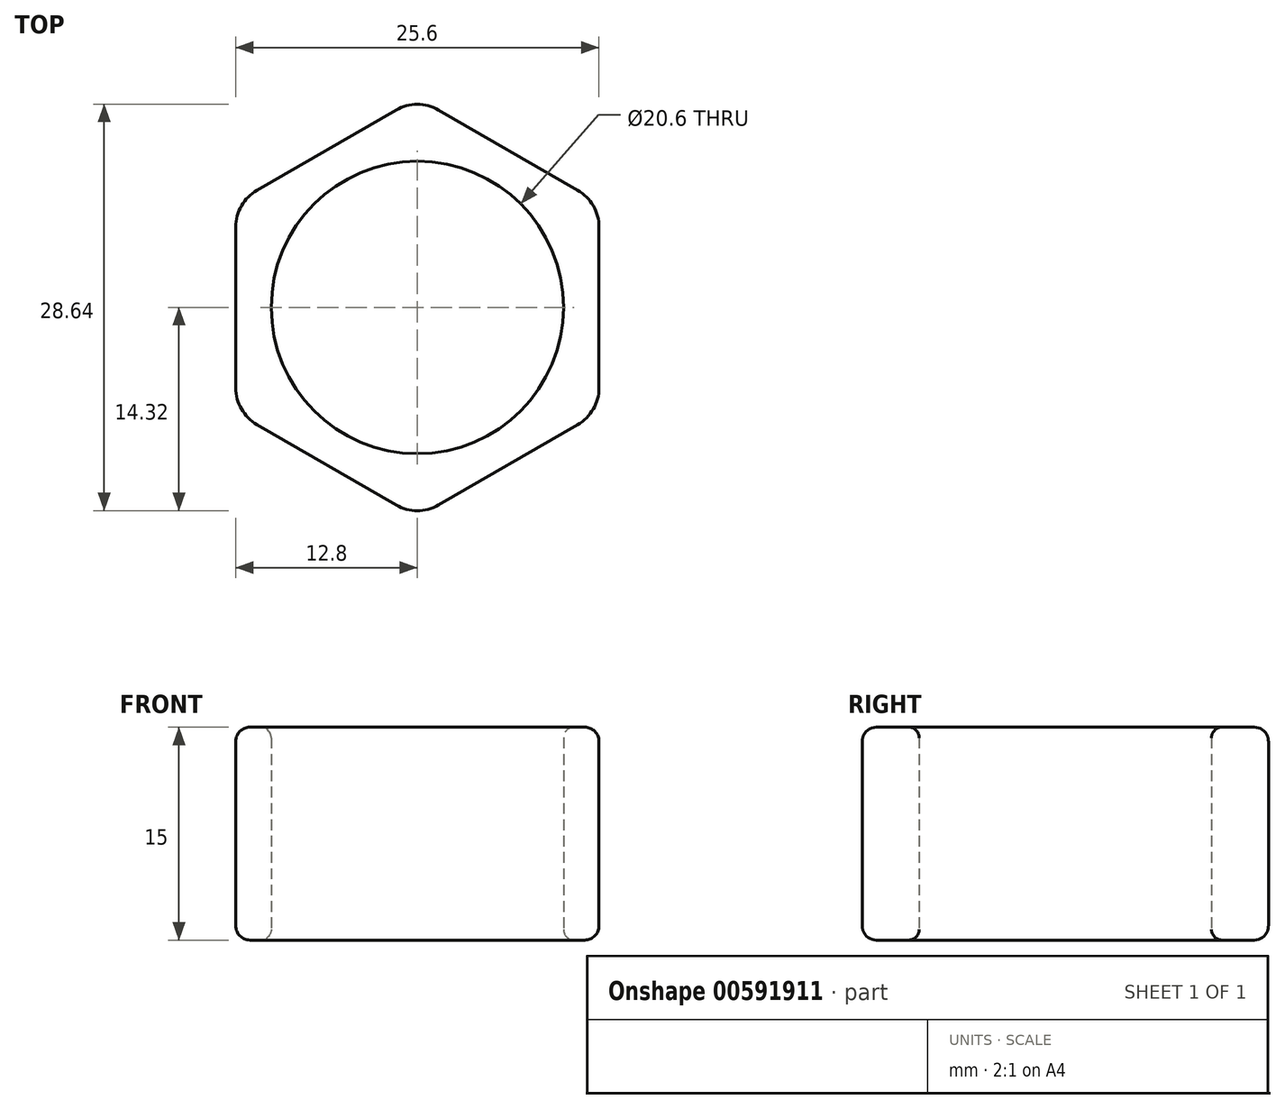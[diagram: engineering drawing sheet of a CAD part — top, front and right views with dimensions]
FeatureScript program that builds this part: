
annotation { "Feature Type Name" : "Feature", "Feature Type Description" : "" }
export const myFeature = defineFeature(function(context is Context, id is Id, definition is map)
    precondition{}
    {
        {
            var Q0;
            Q0=qCreatedBy(makeId("Top.planeOp"),FACE);
            var sketch = newSketch(context, id + "F0", { "sketchPlane" : qUnion([Q0])});
            skCircle(sketch, "E0", {"center": v(0, 0) * mm, "radius": 10.3 * mm});
            skCircle(sketch, "E1.0", {"center": v(0, 0) * mm, "radius": 12.8 * mm});
            skCircle(sketch, "E2.cCircle", {"center": v(0, 0) * mm, "radius": 12.8 * mm, "construction": true});
            skLineSegment(sketch, "E2.0", {"start": v(12.8, 7.4) * mm, "end": v(12.8, -7.4) * mm});
            skLineSegment(sketch, "E2.1", {"start": v(12.8, -7.4) * mm, "end": v(0, -14.78) * mm});
            skLineSegment(sketch, "E2.2", {"start": v(0, -14.78) * mm, "end": v(-12.8, -7.4) * mm});
            skLineSegment(sketch, "E2.3", {"start": v(-12.8, -7.4) * mm, "end": v(-12.8, 7.4) * mm});
            skLineSegment(sketch, "E2.4", {"start": v(-12.8, 7.4) * mm, "end": v(0, 14.78) * mm});
            skLineSegment(sketch, "E2.5", {"start": v(0, 14.78) * mm, "end": v(12.8, 7.4) * mm});
            skPoint(sketch, "E2.0.midPoint", {"position": v(12.8, 0) * mm});
            skSolve(sketch);
        }
        {
            var Q0;
            {var subQ0=sQuery(id+"F0.wireOp",EDGE,"E2.5");var subQ1=sQuery(id+"F0.wireOp",EDGE,"E1.0");var subQ2=makeQuery(id+"F0.imprint","INTERSECT",VERTEX,{"derivedFrom":[subQ1,subQ0]});Q0=makeQuery(id+"F0.imprint","IMPRINT",FACE,{"disambiguationData":[TD([[makeQuery(id+"F0.imprint","IMPRINT",EDGE,{"disambiguationData":[TD([[subQ2,1.0]])],"derivedFrom":subQ1}),-1.0]])]});}
            var Q1;
            {var subQ0=sQuery(id+"F0.wireOp",EDGE,"E2.5");var subQ1=sQuery(id+"F0.wireOp",EDGE,"E1.0");var subQ2=makeQuery(id+"F0.imprint","INTERSECT",VERTEX,{"derivedFrom":[subQ1,subQ0]});Q1=makeQuery(id+"F0.imprint","IMPRINT",FACE,{"disambiguationData":[TD([[makeQuery(id+"F0.imprint","IMPRINT",EDGE,{"disambiguationData":[TD([[subQ2,-1.0]])],"derivedFrom":subQ1}),-1.0]])]});}
            var Q2;
            {var subQ0=sQuery(id+"F0.wireOp",EDGE,"E2.4");var subQ1=sQuery(id+"F0.wireOp",EDGE,"E1.0");var subQ2=makeQuery(id+"F0.imprint","INTERSECT",VERTEX,{"derivedFrom":[subQ1,subQ0]});Q2=makeQuery(id+"F0.imprint","IMPRINT",FACE,{"disambiguationData":[TD([[makeQuery(id+"F0.imprint","IMPRINT",EDGE,{"disambiguationData":[TD([[subQ2,-1.0]])],"derivedFrom":subQ1}),-1.0]])]});}
            var Q3;
            {var subQ0=sQuery(id+"F0.wireOp",EDGE,"E2.3");var subQ1=sQuery(id+"F0.wireOp",EDGE,"E1.0");var subQ2=makeQuery(id+"F0.imprint","INTERSECT",VERTEX,{"derivedFrom":[subQ1,subQ0]});Q3=makeQuery(id+"F0.imprint","IMPRINT",FACE,{"disambiguationData":[TD([[makeQuery(id+"F0.imprint","IMPRINT",EDGE,{"disambiguationData":[TD([[subQ2,-1.0]])],"derivedFrom":subQ1}),-1.0]])]});}
            var Q4;
            {var subQ0=sQuery(id+"F0.wireOp",EDGE,"E2.2");var subQ1=sQuery(id+"F0.wireOp",EDGE,"E1.0");var subQ2=makeQuery(id+"F0.imprint","INTERSECT",VERTEX,{"derivedFrom":[subQ1,subQ0]});Q4=makeQuery(id+"F0.imprint","IMPRINT",FACE,{"disambiguationData":[TD([[makeQuery(id+"F0.imprint","IMPRINT",EDGE,{"disambiguationData":[TD([[subQ2,-1.0]])],"derivedFrom":subQ1}),-1.0]])]});}
            var Q5;
            {var subQ0=sQuery(id+"F0.wireOp",EDGE,"E2.0");var subQ1=sQuery(id+"F0.wireOp",EDGE,"E1.0");var subQ2=makeQuery(id+"F0.imprint","INTERSECT",VERTEX,{"derivedFrom":[subQ1,subQ0]});Q5=makeQuery(id+"F0.imprint","IMPRINT",FACE,{"disambiguationData":[TD([[makeQuery(id+"F0.imprint","IMPRINT",EDGE,{"disambiguationData":[TD([[subQ2,1.0]])],"derivedFrom":subQ1}),-1.0]])]});}
            var Q6;
            Q6=makeQuery(id+"F0.imprint","IMPRINT",FACE,{"disambiguationData":[TD([[makeQuery(id+"F0.imprint","IMPRINT",EDGE,{"derivedFrom":sQuery(id+"F0.wireOp",EDGE,"E0")}),-1.0]])]});
            extrude(context, id + "F1", {"entities" : qUnion([Q0, Q1, Q2, Q3, Q4, Q5, Q6]), "depth" : 15 * mm, "offsetDistance" : 25 * mm});
        }
        {
            var Q0;
            Q0=makeQuery(id+"F1.opExtrude","SWEPT_EDGE",EDGE,{"disambiguationData":[OSD([sQuery(id+"F0.wireOp",EDGE,"E2.4"),sQuery(id+"F0.wireOp",EDGE,"E2.5")])]});
            var Q1;
            Q1=makeQuery(id+"F1.opExtrude","SWEPT_EDGE",EDGE,{"disambiguationData":[OSD([sQuery(id+"F0.wireOp",EDGE,"E2.0"),sQuery(id+"F0.wireOp",EDGE,"E2.5")])]});
            var Q2;
            Q2=makeQuery(id+"F1.opExtrude","SWEPT_EDGE",EDGE,{"disambiguationData":[OSD([sQuery(id+"F0.wireOp",EDGE,"E2.0"),sQuery(id+"F0.wireOp",EDGE,"E2.1")])]});
            var Q3;
            Q3=makeQuery(id+"F1.opExtrude","SWEPT_EDGE",EDGE,{"disambiguationData":[OSD([sQuery(id+"F0.wireOp",EDGE,"E2.1"),sQuery(id+"F0.wireOp",EDGE,"E2.2")])]});
            var Q4;
            Q4=makeQuery(id+"F1.opExtrude","SWEPT_EDGE",EDGE,{"disambiguationData":[OSD([sQuery(id+"F0.wireOp",EDGE,"E2.2"),sQuery(id+"F0.wireOp",EDGE,"E2.3")])]});
            var Q5;
            Q5=makeQuery(id+"F1.opExtrude","SWEPT_EDGE",EDGE,{"disambiguationData":[OSD([sQuery(id+"F0.wireOp",EDGE,"E2.3"),sQuery(id+"F0.wireOp",EDGE,"E2.4")])]});
            fillet(context, id + "F2", {"entities" : qUnion([Q0, Q1, Q2, Q3, Q4, Q5]), "radius" : 3 * mm, "tangentPropagation" : true, "allowEdgeOverflow" : false});
        }
        {
            var Q0;
            Q0=makeQuery(id+"F1.opExtrude","CAP_EDGE",EDGE,{"disambiguationData":[OSD([sQuery(id+"F0.wireOp",EDGE,"E2.0")])],"isStart":false});
            var Q1;
            {var subQ0=sQuery(id+"F0.wireOp",EDGE,"E2.1");var subQ1=sQuery(id+"F0.wireOp",EDGE,"E2.0");Q1=makeQuery(id+"F2.opFillet","BLEND_EDGE",EDGE,{"blendedFrom":[makeQuery(id+"F1.opExtrude","SWEPT_EDGE",EDGE,{"disambiguationData":[OSD([subQ1,subQ0])]}),makeQuery(id+"F1.opExtrude","CAP_FACE",FACE,{"disambiguationData":[OSD([sQuery(id+"F0.wireOp",EDGE,"E0"),subQ1,subQ0,sQuery(id+"F0.wireOp",EDGE,"E2.2"),sQuery(id+"F0.wireOp",EDGE,"E2.3"),sQuery(id+"F0.wireOp",EDGE,"E2.4"),sQuery(id+"F0.wireOp",EDGE,"E2.5")])],"isStart":false})],"blendedInto":[makeQuery(id+"F1.opExtrude","CAP_FACE",FACE,{"disambiguationData":[OSD([sQuery(id+"F0.wireOp",EDGE,"E0"),subQ1,subQ0,sQuery(id+"F0.wireOp",EDGE,"E2.2"),sQuery(id+"F0.wireOp",EDGE,"E2.3"),sQuery(id+"F0.wireOp",EDGE,"E2.4"),sQuery(id+"F0.wireOp",EDGE,"E2.5")])],"isStart":false})]});}
            var Q2;
            Q2=makeQuery(id+"F1.opExtrude","CAP_EDGE",EDGE,{"disambiguationData":[OSD([sQuery(id+"F0.wireOp",EDGE,"E2.1")])],"isStart":false});
            var Q3;
            Q3=makeQuery(id+"F1.opExtrude","CAP_EDGE",EDGE,{"disambiguationData":[OSD([sQuery(id+"F0.wireOp",EDGE,"E2.2")])],"isStart":false});
            var Q4;
            {var subQ0=sQuery(id+"F0.wireOp",EDGE,"E2.3");var subQ1=sQuery(id+"F0.wireOp",EDGE,"E2.2");Q4=makeQuery(id+"F2.opFillet","BLEND_EDGE",EDGE,{"blendedFrom":[makeQuery(id+"F1.opExtrude","SWEPT_EDGE",EDGE,{"disambiguationData":[OSD([subQ1,subQ0])]}),makeQuery(id+"F1.opExtrude","CAP_FACE",FACE,{"disambiguationData":[OSD([sQuery(id+"F0.wireOp",EDGE,"E0"),sQuery(id+"F0.wireOp",EDGE,"E2.0"),sQuery(id+"F0.wireOp",EDGE,"E2.1"),subQ1,subQ0,sQuery(id+"F0.wireOp",EDGE,"E2.4"),sQuery(id+"F0.wireOp",EDGE,"E2.5")])],"isStart":false})],"blendedInto":[makeQuery(id+"F1.opExtrude","CAP_FACE",FACE,{"disambiguationData":[OSD([sQuery(id+"F0.wireOp",EDGE,"E0"),sQuery(id+"F0.wireOp",EDGE,"E2.0"),sQuery(id+"F0.wireOp",EDGE,"E2.1"),subQ1,subQ0,sQuery(id+"F0.wireOp",EDGE,"E2.4"),sQuery(id+"F0.wireOp",EDGE,"E2.5")])],"isStart":false})]});}
            var Q5;
            Q5=makeQuery(id+"F1.opExtrude","CAP_EDGE",EDGE,{"disambiguationData":[OSD([sQuery(id+"F0.wireOp",EDGE,"E2.3")])],"isStart":false});
            var Q6;
            {var subQ0=sQuery(id+"F0.wireOp",EDGE,"E2.4");var subQ1=sQuery(id+"F0.wireOp",EDGE,"E2.3");Q6=makeQuery(id+"F2.opFillet","BLEND_EDGE",EDGE,{"blendedFrom":[makeQuery(id+"F1.opExtrude","SWEPT_EDGE",EDGE,{"disambiguationData":[OSD([subQ1,subQ0])]}),makeQuery(id+"F1.opExtrude","CAP_FACE",FACE,{"disambiguationData":[OSD([sQuery(id+"F0.wireOp",EDGE,"E0"),sQuery(id+"F0.wireOp",EDGE,"E2.0"),sQuery(id+"F0.wireOp",EDGE,"E2.1"),sQuery(id+"F0.wireOp",EDGE,"E2.2"),subQ1,subQ0,sQuery(id+"F0.wireOp",EDGE,"E2.5")])],"isStart":false})],"blendedInto":[makeQuery(id+"F1.opExtrude","CAP_FACE",FACE,{"disambiguationData":[OSD([sQuery(id+"F0.wireOp",EDGE,"E0"),sQuery(id+"F0.wireOp",EDGE,"E2.0"),sQuery(id+"F0.wireOp",EDGE,"E2.1"),sQuery(id+"F0.wireOp",EDGE,"E2.2"),subQ1,subQ0,sQuery(id+"F0.wireOp",EDGE,"E2.5")])],"isStart":false})]});}
            var Q7;
            Q7=makeQuery(id+"F1.opExtrude","CAP_EDGE",EDGE,{"disambiguationData":[OSD([sQuery(id+"F0.wireOp",EDGE,"E2.4")])],"isStart":false});
            var Q8;
            Q8=makeQuery(id+"F1.opExtrude","CAP_EDGE",EDGE,{"disambiguationData":[OSD([sQuery(id+"F0.wireOp",EDGE,"E2.5")])],"isStart":false});
            var Q9;
            {var subQ0=sQuery(id+"F0.wireOp",EDGE,"E2.2");var subQ1=sQuery(id+"F0.wireOp",EDGE,"E2.1");Q9=makeQuery(id+"F2.opFillet","BLEND_EDGE",EDGE,{"blendedFrom":[makeQuery(id+"F1.opExtrude","SWEPT_EDGE",EDGE,{"disambiguationData":[OSD([subQ1,subQ0])]}),makeQuery(id+"F1.opExtrude","CAP_FACE",FACE,{"disambiguationData":[OSD([sQuery(id+"F0.wireOp",EDGE,"E0"),sQuery(id+"F0.wireOp",EDGE,"E2.0"),subQ1,subQ0,sQuery(id+"F0.wireOp",EDGE,"E2.3"),sQuery(id+"F0.wireOp",EDGE,"E2.4"),sQuery(id+"F0.wireOp",EDGE,"E2.5")])],"isStart":false})],"blendedInto":[makeQuery(id+"F1.opExtrude","CAP_FACE",FACE,{"disambiguationData":[OSD([sQuery(id+"F0.wireOp",EDGE,"E0"),sQuery(id+"F0.wireOp",EDGE,"E2.0"),subQ1,subQ0,sQuery(id+"F0.wireOp",EDGE,"E2.3"),sQuery(id+"F0.wireOp",EDGE,"E2.4"),sQuery(id+"F0.wireOp",EDGE,"E2.5")])],"isStart":false})]});}
            var Q10;
            {var subQ0=sQuery(id+"F0.wireOp",EDGE,"E2.5");var subQ1=sQuery(id+"F0.wireOp",EDGE,"E2.4");Q10=makeQuery(id+"F2.opFillet","BLEND_EDGE",EDGE,{"blendedFrom":[makeQuery(id+"F1.opExtrude","SWEPT_EDGE",EDGE,{"disambiguationData":[OSD([subQ1,subQ0])]}),makeQuery(id+"F1.opExtrude","CAP_FACE",FACE,{"disambiguationData":[OSD([sQuery(id+"F0.wireOp",EDGE,"E0"),sQuery(id+"F0.wireOp",EDGE,"E2.0"),sQuery(id+"F0.wireOp",EDGE,"E2.1"),sQuery(id+"F0.wireOp",EDGE,"E2.2"),sQuery(id+"F0.wireOp",EDGE,"E2.3"),subQ1,subQ0])],"isStart":false})],"blendedInto":[makeQuery(id+"F1.opExtrude","CAP_FACE",FACE,{"disambiguationData":[OSD([sQuery(id+"F0.wireOp",EDGE,"E0"),sQuery(id+"F0.wireOp",EDGE,"E2.0"),sQuery(id+"F0.wireOp",EDGE,"E2.1"),sQuery(id+"F0.wireOp",EDGE,"E2.2"),sQuery(id+"F0.wireOp",EDGE,"E2.3"),subQ1,subQ0])],"isStart":false})]});}
            var Q11;
            {var subQ0=sQuery(id+"F0.wireOp",EDGE,"E2.5");var subQ1=sQuery(id+"F0.wireOp",EDGE,"E2.0");Q11=makeQuery(id+"F2.opFillet","BLEND_EDGE",EDGE,{"blendedFrom":[makeQuery(id+"F1.opExtrude","SWEPT_EDGE",EDGE,{"disambiguationData":[OSD([subQ1,subQ0])]}),makeQuery(id+"F1.opExtrude","CAP_FACE",FACE,{"disambiguationData":[OSD([sQuery(id+"F0.wireOp",EDGE,"E0"),subQ1,sQuery(id+"F0.wireOp",EDGE,"E2.1"),sQuery(id+"F0.wireOp",EDGE,"E2.2"),sQuery(id+"F0.wireOp",EDGE,"E2.3"),sQuery(id+"F0.wireOp",EDGE,"E2.4"),subQ0])],"isStart":false})],"blendedInto":[makeQuery(id+"F1.opExtrude","CAP_FACE",FACE,{"disambiguationData":[OSD([sQuery(id+"F0.wireOp",EDGE,"E0"),subQ1,sQuery(id+"F0.wireOp",EDGE,"E2.1"),sQuery(id+"F0.wireOp",EDGE,"E2.2"),sQuery(id+"F0.wireOp",EDGE,"E2.3"),sQuery(id+"F0.wireOp",EDGE,"E2.4"),subQ0])],"isStart":false})]});}
            var Q12;
            Q12=makeQuery(id+"F1.opExtrude","CAP_EDGE",EDGE,{"disambiguationData":[OSD([sQuery(id+"F0.wireOp",EDGE,"E2.2")])],"isStart":true});
            var Q13;
            {var subQ0=sQuery(id+"F0.wireOp",EDGE,"E2.2");var subQ1=sQuery(id+"F0.wireOp",EDGE,"E2.1");Q13=makeQuery(id+"F2.opFillet","BLEND_EDGE",EDGE,{"blendedFrom":[makeQuery(id+"F1.opExtrude","SWEPT_EDGE",EDGE,{"disambiguationData":[OSD([subQ1,subQ0])]}),makeQuery(id+"F1.opExtrude","CAP_FACE",FACE,{"disambiguationData":[OSD([sQuery(id+"F0.wireOp",EDGE,"E0"),sQuery(id+"F0.wireOp",EDGE,"E2.0"),subQ1,subQ0,sQuery(id+"F0.wireOp",EDGE,"E2.3"),sQuery(id+"F0.wireOp",EDGE,"E2.4"),sQuery(id+"F0.wireOp",EDGE,"E2.5")])],"isStart":true})],"blendedInto":[makeQuery(id+"F1.opExtrude","CAP_FACE",FACE,{"disambiguationData":[OSD([sQuery(id+"F0.wireOp",EDGE,"E0"),sQuery(id+"F0.wireOp",EDGE,"E2.0"),subQ1,subQ0,sQuery(id+"F0.wireOp",EDGE,"E2.3"),sQuery(id+"F0.wireOp",EDGE,"E2.4"),sQuery(id+"F0.wireOp",EDGE,"E2.5")])],"isStart":true})]});}
            fillet(context, id + "F3", {"entities" : qUnion([Q0, Q1, Q2, Q3, Q4, Q5, Q6, Q7, Q8, Q9, Q10, Q11, Q12, Q13]), "radius" : 1 * mm, "tangentPropagation" : true, "allowEdgeOverflow" : false});
        }
        {
            var Q0;
            Q0=makeQuery(id+"F1.opExtrude","CAP_EDGE",EDGE,{"disambiguationData":[OSD([sQuery(id+"F0.wireOp",EDGE,"E0")])],"isStart":true});
            var Q1;
            Q1=makeQuery(id+"F1.opExtrude","CAP_EDGE",EDGE,{"disambiguationData":[OSD([sQuery(id+"F0.wireOp",EDGE,"E0")])],"isStart":false});
            fillet(context, id + "F4", {"entities" : qUnion([Q0, Q1]), "radius" : 0.75 * mm, "tangentPropagation" : true, "allowEdgeOverflow" : false});
        }
    });
